# Revit family: PCT_клапан
name_source: partatom
category: Арматура воздуховодов
revit_build: Autodesk Revit 2014 (Build: 20140709_2115(x64)
units: mm (PartAtom-declared; Revit-internal decimal feet)

## types (18) — shared parameters
Материал = <По категории>
УГО = УГО(INPLAST)

## per-type parameters (varying)
| type | Aef | d | x | y | Вес | Тип привода |
| PCT-200-T1 | 30000 мм² | 200 мм | 100 мм | 110 мм | 1.5 | 1 |
| PCT-250-T1 | 50000 мм² | 250 мм | 125 мм | 135 мм | 2.3 | 1 |
| PCT-315-T1 | 80000 мм² | 315 мм | 158 мм | 168 мм | 3.6 | 1 |
| PCT-400-T1 | 130000 мм² | 400 мм | 200 мм | 210 мм | 5.8 | 1 |
| PCT-500-T1 | 200000 мм² | 500 мм | 250 мм | 260 мм | 9.6 | 1 |
| PCT-630-T1 | 300000 мм² | 630 мм | 315 мм | 325 мм | 15 | 1 |
| PCT-200-T2 | 30000 мм² | 200 мм | 100 мм | 110 мм | 1.5 | 2 |
| PCT-250-T2 | 50000 мм² | 250 мм | 125 мм | 135 мм | 2.3 | 2 |
| PCT-315-T2 | 80000 мм² | 315 мм | 158 мм | 168 мм | 3.6 | 2 |
| PCT-400-T2 | 130000 мм² | 400 мм | 200 мм | 210 мм | 5.8 | 2 |
| PCT-500-T2 | 200000 мм² | 500 мм | 250 мм | 260 мм | 9.6 | 2 |
| PCT-630-T2 | 300000 мм² | 630 мм | 315 мм | 325 мм | 15 | 2 |
| PCT-200-T3 | 30000 мм² | 200 мм | 100 мм | 110 мм | 1.5 | 3 |
| PCT-250-T3 | 50000 мм² | 250 мм | 125 мм | 135 мм | 2.3 | 3 |
| PCT-315-T3 | 80000 мм² | 315 мм | 158 мм | 168 мм | 3.6 | 3 |
| PCT-400-T3 | 130000 мм² | 400 мм | 200 мм | 210 мм | 5.8 | 3 |
| PCT-500-T3 | 200000 мм² | 500 мм | 250 мм | 260 мм | 9.6 | 3 |
| PCT-630-T3 | 300000 мм² | 630 мм | 315 мм | 325 мм | 15 | 3 |

note: column(s) folded — value = type name in every type: Комментарии к типоразмеру
